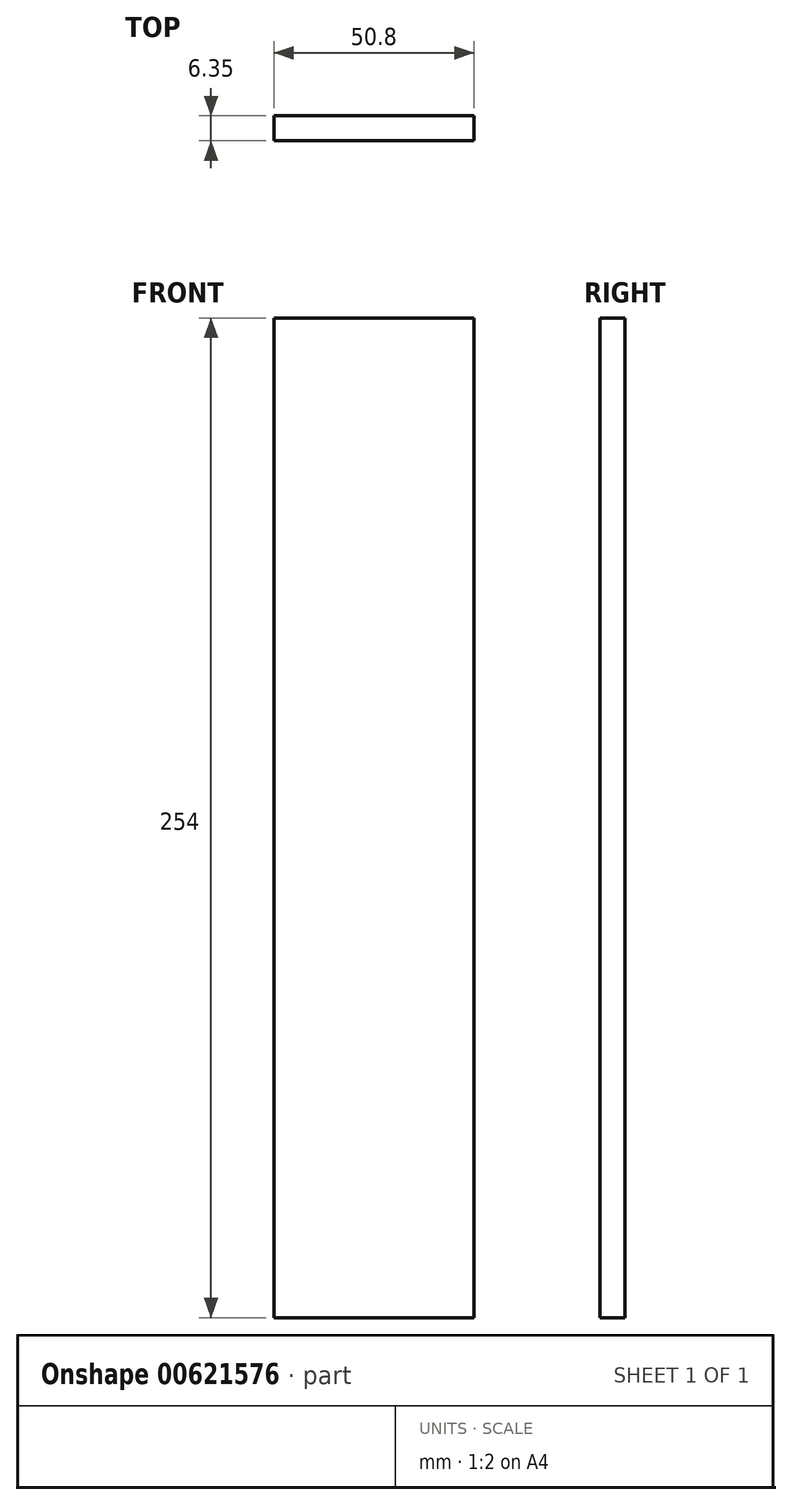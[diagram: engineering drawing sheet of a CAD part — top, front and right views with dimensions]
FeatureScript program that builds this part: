
annotation { "Feature Type Name" : "Feature", "Feature Type Description" : "" }
export const myFeature = defineFeature(function(context is Context, id is Id, definition is map)
    precondition{}
    {
        {
            var Q0;
            Q0=qCreatedBy(makeId("Front.planeOp"),FACE);
            var sketch = newSketch(context, id + "F0", { "sketchPlane" : qUnion([Q0])});
            skLineSegment(sketch, "E0.bottom", {"start": v(25.4, 127) * mm, "end": v(-25.4, 127) * mm});
            skLineSegment(sketch, "E0.top", {"start": v(25.4, -127) * mm, "end": v(-25.4, -127) * mm});
            skLineSegment(sketch, "E0.left", {"start": v(25.4, 127) * mm, "end": v(25.4, -127) * mm});
            skLineSegment(sketch, "E0.right", {"start": v(-25.4, 127) * mm, "end": v(-25.4, -127) * mm});
            skPoint(sketch, "E0.middle", {"position": v(0, 0) * mm});
            skSolve(sketch);
        }
        {
            var Q0;
            Q0 = qSketchRegion(id + "F0", true);
            extrude(context, id + "F1", {"entities" : qUnion([Q0]), "depth" : 6.35 * mm, "offsetDistance" : 25.4 * mm});
        }
    });
